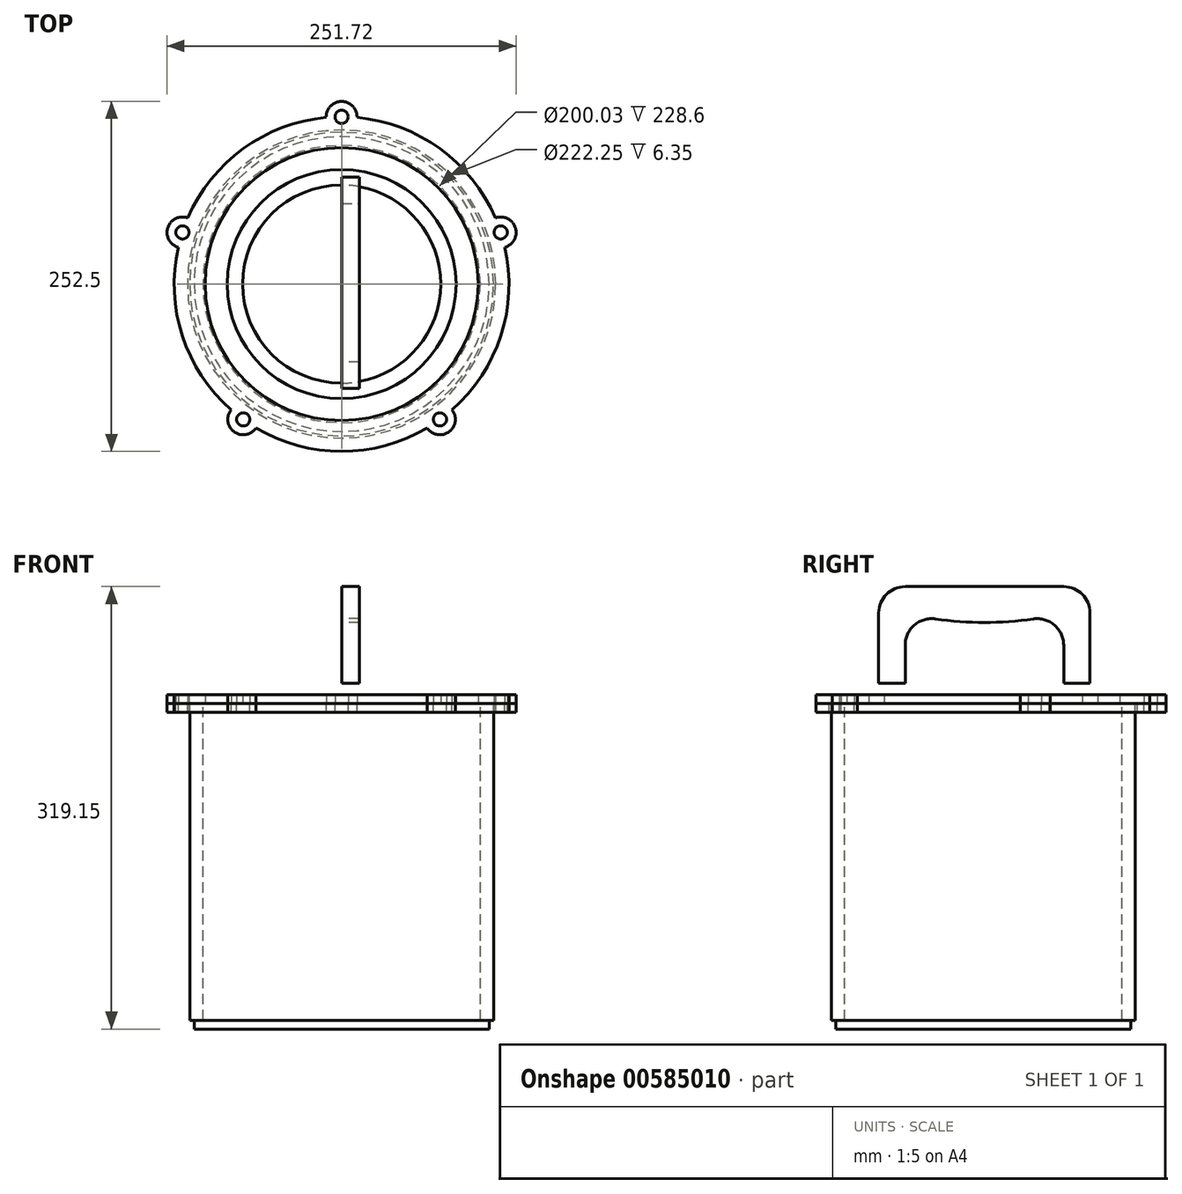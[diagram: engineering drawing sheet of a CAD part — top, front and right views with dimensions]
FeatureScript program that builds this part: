
annotation { "Feature Type Name" : "Feature", "Feature Type Description" : "" }
export const myFeature = defineFeature(function(context is Context, id is Id, definition is map)
    precondition{}
    {
        {
            var Q0;
            Q0=qCreatedBy(makeId("Top.planeOp"),FACE);
            var sketch = newSketch(context, id + "F0", { "sketchPlane" : qUnion([Q0])});
            skCircle(sketch, "E0", {"center": v(0, 0) * mm, "radius": 131.76 * mm, "construction": true});
            skCircle(sketch, "E1", {"center": v(0, 0) * mm, "radius": 109.54 * mm, "construction": true});
            skLineSegment(sketch, "E2", {"start": v(0, 0) * mm, "end": v(0, 120.65) * mm, "construction": true});
            skCircle(sketch, "E3", {"center": v(0, 120.65) * mm, "radius": 4.76 * mm});
            skArc(sketch, "E4", {"start": v(11.1, 120.23) * mm, "mid": v(-0.05, 131.76) * mm, "end": v(-11.1, 120.14) * mm});
            skArc(sketch, "E5.1.0", {"start": v(-110.92, 47.71) * mm, "mid": v(-125.33, 40.67) * mm, "end": v(-117.69, 26.57) * mm});
            skCircle(sketch, "E5.1.1", {"center": v(-114.74, 37.28) * mm, "radius": 4.76 * mm});
            skArc(sketch, "E5.2.0", {"start": v(-79.65, -90.74) * mm, "mid": v(-77.4, -106.63) * mm, "end": v(-61.63, -103.72) * mm});
            skCircle(sketch, "E5.2.1", {"center": v(-70.92, -97.6) * mm, "radius": 4.76 * mm});
            skArc(sketch, "E6.3.3.0", {"start": v(61.69, -103.8) * mm, "mid": v(77.49, -106.57) * mm, "end": v(79.6, -90.67) * mm});
            skCircle(sketch, "E6.4.3.0", {"center": v(70.92, -97.6) * mm, "radius": 4.76 * mm});
            skArc(sketch, "E6.3.4.0", {"start": v(117.78, 26.6) * mm, "mid": v(125.3, 40.76) * mm, "end": v(110.83, 47.68) * mm});
            skCircle(sketch, "E6.4.4.0", {"center": v(114.74, 37.28) * mm, "radius": 4.76 * mm});
            skArc(sketch, "E7", {"start": v(-110.92, 47.71) * mm, "mid": v(-70.97, 97.68) * mm, "end": v(-11.1, 120.23) * mm});
            skArc(sketch, "E8.1.0", {"start": v(-79.65, -90.74) * mm, "mid": v(-114.83, -37.31) * mm, "end": v(-117.78, 26.6) * mm});
            skArc(sketch, "E8.2.0", {"start": v(61.69, -103.8) * mm, "mid": v(0, -120.74) * mm, "end": v(-61.69, -103.8) * mm});
            skArc(sketch, "E8.3.0", {"start": v(117.78, 26.6) * mm, "mid": v(114.83, -37.31) * mm, "end": v(79.65, -90.74) * mm});
            skArc(sketch, "E8.4.0", {"start": v(11.1, 120.23) * mm, "mid": v(70.97, 97.68) * mm, "end": v(110.92, 47.71) * mm});
            skSolve(sketch);
        }
        {
            var Q0;
            Q0 = qSketchRegion(id + "F0", true);
            extrude(context, id + "F1", {"entities" : qUnion([Q0]), "depth" : 6.35 * mm, "offsetDistance" : 25.4 * mm});
        }
        {
            var Q0;
            Q0=qCreatedBy(makeId("Right.planeOp"),FACE);
            var sketch = newSketch(context, id + "F2", { "sketchPlane" : qUnion([Q0])});
            skLineSegment(sketch, "E9.bottom", {"start": v(-56.3, 65.15) * mm, "end": v(58, 65.15) * mm, "construction": true});
            skLineSegment(sketch, "E9.top", {"start": v(-56.3, 14.35) * mm, "end": v(58, 14.35) * mm, "construction": true});
            skLineSegment(sketch, "E9.left", {"start": v(-56.3, 65.15) * mm, "end": v(-56.3, 14.35) * mm});
            skLineSegment(sketch, "E9.right", {"start": v(58, 65.15) * mm, "end": v(58, 14.35) * mm});
            skLineSegment(sketch, "E10.bottom", {"start": v(-75.36, 14.35) * mm, "end": v(77.04, 14.35) * mm});
            skLineSegment(sketch, "E10.top", {"start": v(-75.36, 84.2) * mm, "end": v(77.04, 84.2) * mm});
            skLineSegment(sketch, "E10.left", {"start": v(-75.36, 14.35) * mm, "end": v(-75.36, 84.2) * mm});
            skLineSegment(sketch, "E10.right", {"start": v(77.04, 14.35) * mm, "end": v(77.04, 84.2) * mm});
            skLineSegment(sketch, "E11", {"start": v(0.84, 65.15) * mm, "end": v(0.84, 47.46) * mm, "construction": true});
            skArc(sketch, "E12", {"start": v(-56.3, 65.15) * mm, "mid": v(0.84, 58.3) * mm, "end": v(58, 65.15) * mm});
            skSolve(sketch);
        }
        {
            var Q0;
            {var subQ1=sQuery(id+"F2.wireOp",EDGE,"E9.left");Q0=makeQuery(id+"F2.imprint","IMPRINT",FACE,{"disambiguationData":[TD([[makeQuery(id+"F2.imprint","IMPRINT",EDGE,{"derivedFrom":subQ1}),-1.0]])]});}
            extrude(context, id + "F3", {"entities" : qUnion([Q0]), "depth" : 12.7 * mm, "offsetDistance" : 25.4 * mm});
        }
        {
            var Q0;
            Q0=makeQuery(id+"F3.opExtrude","SWEPT_EDGE",EDGE,{"disambiguationData":[OSD([sQuery(id+"F2.wireOp",EDGE,"E10.top"),sQuery(id+"F2.wireOp",EDGE,"E10.left")])]});
            var Q1;
            Q1=makeQuery(id+"F3.opExtrude","SWEPT_EDGE",EDGE,{"disambiguationData":[OSD([sQuery(id+"F2.wireOp",EDGE,"E10.top"),sQuery(id+"F2.wireOp",EDGE,"E10.right")])]});
            var Q2;
            Q2=makeQuery(id+"F3.opExtrude","SWEPT_EDGE",EDGE,{"disambiguationData":[OSD([sQuery(id+"F2.wireOp",EDGE,"E9.left"),sQuery(id+"F2.wireOp",EDGE,"E12")])]});
            var Q3;
            Q3=makeQuery(id+"F3.opExtrude","SWEPT_EDGE",EDGE,{"disambiguationData":[OSD([sQuery(id+"F2.wireOp",EDGE,"E9.right"),sQuery(id+"F2.wireOp",EDGE,"E12")])]});
            fillet(context, id + "F4", {"entities" : qUnion([Q0, Q1, Q2, Q3]), "tangentPropagation" : true, "radius" : 19.05 * mm, "defaultsChanged" : true, "vertexSettings" : [], "allowEdgeOverflow" : false});
        }
        {
            var Q0;
            Q0=makeQuery(id+"F1.opExtrude","CAP_FACE",FACE,{"disambiguationData":[OSD([sQuery(id+"F0.wireOp",EDGE,"E3"),sQuery(id+"F0.wireOp",EDGE,"E4"),sQuery(id+"F0.wireOp",EDGE,"E5.1.0"),sQuery(id+"F0.wireOp",EDGE,"E5.1.1"),sQuery(id+"F0.wireOp",EDGE,"E5.2.0"),sQuery(id+"F0.wireOp",EDGE,"E5.2.1"),sQuery(id+"F0.wireOp",EDGE,"E6.3.3.0"),sQuery(id+"F0.wireOp",EDGE,"E6.4.3.0"),sQuery(id+"F0.wireOp",EDGE,"E6.3.4.0"),sQuery(id+"F0.wireOp",EDGE,"E6.4.4.0"),sQuery(id+"F0.wireOp",EDGE,"E7"),sQuery(id+"F0.wireOp",EDGE,"E8.1.0"),sQuery(id+"F0.wireOp",EDGE,"E8.2.0"),sQuery(id+"F0.wireOp",EDGE,"E8.3.0"),sQuery(id+"F0.wireOp",EDGE,"E8.4.0")])],"isStart":true});
            var sketch = newSketch(context, id + "F5", { "sketchPlane" : qUnion([Q0])});
            skCircle(sketch, "E13", {"center": v(0, 0) * mm, "radius": 131.76 * mm, "construction": true});
            skCircle(sketch, "E14", {"center": v(0, 0) * mm, "radius": 111.13 * mm});
            skLineSegment(sketch, "E15", {"start": v(0, 0) * mm, "end": v(70.92, 97.6) * mm, "construction": true});
            skCircle(sketch, "E16", {"center": v(70.92, 97.6) * mm, "radius": 4.76 * mm});
            skArc(sketch, "E17", {"start": v(79.65, 90.74) * mm, "mid": v(77.4, 106.63) * mm, "end": v(61.63, 103.72) * mm});
            skArc(sketch, "E18.1.0", {"start": v(-61.69, 103.8) * mm, "mid": v(-77.49, 106.57) * mm, "end": v(-79.6, 90.67) * mm});
            skCircle(sketch, "E18.1.1", {"center": v(-70.92, 97.6) * mm, "radius": 4.76 * mm});
            skArc(sketch, "E18.2.0", {"start": v(-117.78, -26.6) * mm, "mid": v(-125.3, -40.76) * mm, "end": v(-110.83, -47.68) * mm});
            skCircle(sketch, "E18.2.1", {"center": v(-114.74, -37.28) * mm, "radius": 4.76 * mm});
            skArc(sketch, "E19.3.3.0", {"start": v(-11.1, -120.23) * mm, "mid": v(0.05, -131.76) * mm, "end": v(11.1, -120.14) * mm});
            skCircle(sketch, "E19.4.3.0", {"center": v(0, -120.65) * mm, "radius": 4.76 * mm});
            skArc(sketch, "E19.3.4.0", {"start": v(110.92, -47.71) * mm, "mid": v(125.33, -40.67) * mm, "end": v(117.69, -26.57) * mm});
            skCircle(sketch, "E19.4.4.0", {"center": v(114.74, -37.28) * mm, "radius": 4.76 * mm});
            skArc(sketch, "E20", {"start": v(-61.69, 103.8) * mm, "mid": v(0, 120.74) * mm, "end": v(61.69, 103.8) * mm});
            skArc(sketch, "E21.1.0", {"start": v(-117.78, -26.6) * mm, "mid": v(-114.83, 37.31) * mm, "end": v(-79.65, 90.74) * mm});
            skArc(sketch, "E21.2.0", {"start": v(-11.1, -120.23) * mm, "mid": v(-70.97, -97.68) * mm, "end": v(-110.92, -47.71) * mm});
            skArc(sketch, "E21.3.0", {"start": v(110.92, -47.71) * mm, "mid": v(70.97, -97.68) * mm, "end": v(11.1, -120.23) * mm});
            skArc(sketch, "E21.4.0", {"start": v(79.65, 90.74) * mm, "mid": v(114.83, 37.31) * mm, "end": v(117.78, -26.6) * mm});
            skSolve(sketch);
        }
        {
            var Q0;
            Q0 = qSketchRegion(id + "F5", true);
            extrude(context, id + "F6", {"entities" : qUnion([Q0]), "depth" : 6.35 * mm, "offsetDistance" : 25.4 * mm});
        }
        {
            var Q0;
            Q0=makeQuery(id+"F1.opExtrude","CAP_FACE",FACE,{"disambiguationData":[OSD([sQuery(id+"F0.wireOp",EDGE,"E3"),sQuery(id+"F0.wireOp",EDGE,"E4"),sQuery(id+"F0.wireOp",EDGE,"E5.1.0"),sQuery(id+"F0.wireOp",EDGE,"E5.1.1"),sQuery(id+"F0.wireOp",EDGE,"E5.2.0"),sQuery(id+"F0.wireOp",EDGE,"E5.2.1"),sQuery(id+"F0.wireOp",EDGE,"E6.3.3.0"),sQuery(id+"F0.wireOp",EDGE,"E6.4.3.0"),sQuery(id+"F0.wireOp",EDGE,"E6.3.4.0"),sQuery(id+"F0.wireOp",EDGE,"E6.4.4.0"),sQuery(id+"F0.wireOp",EDGE,"E7"),sQuery(id+"F0.wireOp",EDGE,"E8.1.0"),sQuery(id+"F0.wireOp",EDGE,"E8.2.0"),sQuery(id+"F0.wireOp",EDGE,"E8.3.0"),sQuery(id+"F0.wireOp",EDGE,"E8.4.0")])],"isStart":true});
            var sketch = newSketch(context, id + "F7", { "sketchPlane" : qUnion([Q0])});
            skCircle(sketch, "E22", {"center": v(0, 0) * mm, "radius": 109.54 * mm});
            skCircle(sketch, "E23", {"center": v(0, 0) * mm, "radius": 100.01 * mm});
            skSolve(sketch);
        }
        {
            var Q0;
            Q0 = qSketchRegion(id + "F7", true);
            extrude(context, id + "F8", {"entities" : qUnion([Q0]), "depth" : 228.6 * mm, "offsetDistance" : 25.4 * mm});
        }
        {
            var Q0;
            Q0=makeQuery(id+"F8.opExtrude","CAP_FACE",FACE,{"disambiguationData":[OSD([sQuery(id+"F7.wireOp",EDGE,"E22"),sQuery(id+"F7.wireOp",EDGE,"E23")])],"isStart":false});
            var sketch = newSketch(context, id + "F9", { "sketchPlane" : qUnion([Q0])});
            skCircle(sketch, "E24", {"center": v(0, 0) * mm, "radius": 106.36 * mm});
            skSolve(sketch);
        }
        {
            var Q0;
            Q0 = qSketchRegion(id + "F9", true);
            extrude(context, id + "F10", {"entities" : qUnion([Q0]), "depth" : 6.35 * mm, "offsetDistance" : 25.4 * mm});
        }
        {
            var Q0;
            Q0=qCreatedBy(makeId("Top.planeOp"),FACE);
            var sketch = newSketch(context, id + "F11", { "sketchPlane" : qUnion([Q0])});
            skCircle(sketch, "E25", {"center": v(0, 0) * mm, "radius": 100.01 * mm, "construction": true});
            skCircle(sketch, "E26", {"center": v(0, 0) * mm, "radius": 82.55 * mm, "construction": true});
            skCircle(sketch, "E27", {"center": v(0, 0) * mm, "radius": 93.66 * mm});
            skCircle(sketch, "E28", {"center": v(0, 0) * mm, "radius": 76.2 * mm});
            skSolve(sketch);
        }
        {
            var Q0;
            Q0=makeQuery(id+"F11.imprint","IMPRINT",FACE,{"disambiguationData":[TD([[makeQuery(id+"F11.imprint","IMPRINT",EDGE,{"derivedFrom":sQuery(id+"F11.wireOp",EDGE,"E28")}),1.0]])]});
            var sketch = newSketch(context, id + "F12", { "sketchPlane" : qUnion([Q0])});
            skCircle(sketch, "E29", {"center": v(0, 0) * mm, "radius": 98.43 * mm});
            skCircle(sketch, "E30", {"center": v(0, 0) * mm, "radius": 82.55 * mm});
            skSolve(sketch);
        }
        {
            var Q0;
            Q0 = qSketchRegion(id + "F12", true);
            extrude(context, id + "F13", {"entities" : qUnion([Q0]), "depth" : 6.35 * mm, "offsetDistance" : 25.4 * mm});
        }
        {
            var Q0;
            Q0=makeQuery(id+"F11.imprint","IMPRINT",FACE,{"disambiguationData":[TD([[makeQuery(id+"F11.imprint","IMPRINT",EDGE,{"derivedFrom":sQuery(id+"F11.wireOp",EDGE,"E28")}),1.0]])]});
            var sketch = newSketch(context, id + "F14", { "sketchPlane" : qUnion([Q0])});
            skCircle(sketch, "E31", {"center": v(0, 0) * mm, "radius": 71.44 * mm});
            skSolve(sketch);
        }
        {
            var Q0;
            Q0 = qSketchRegion(id + "F14", true);
            extrude(context, id + "F15", {"entities" : qUnion([Q0]), "depth" : 6.35 * mm, "offsetDistance" : 25.4 * mm});
        }
    });
